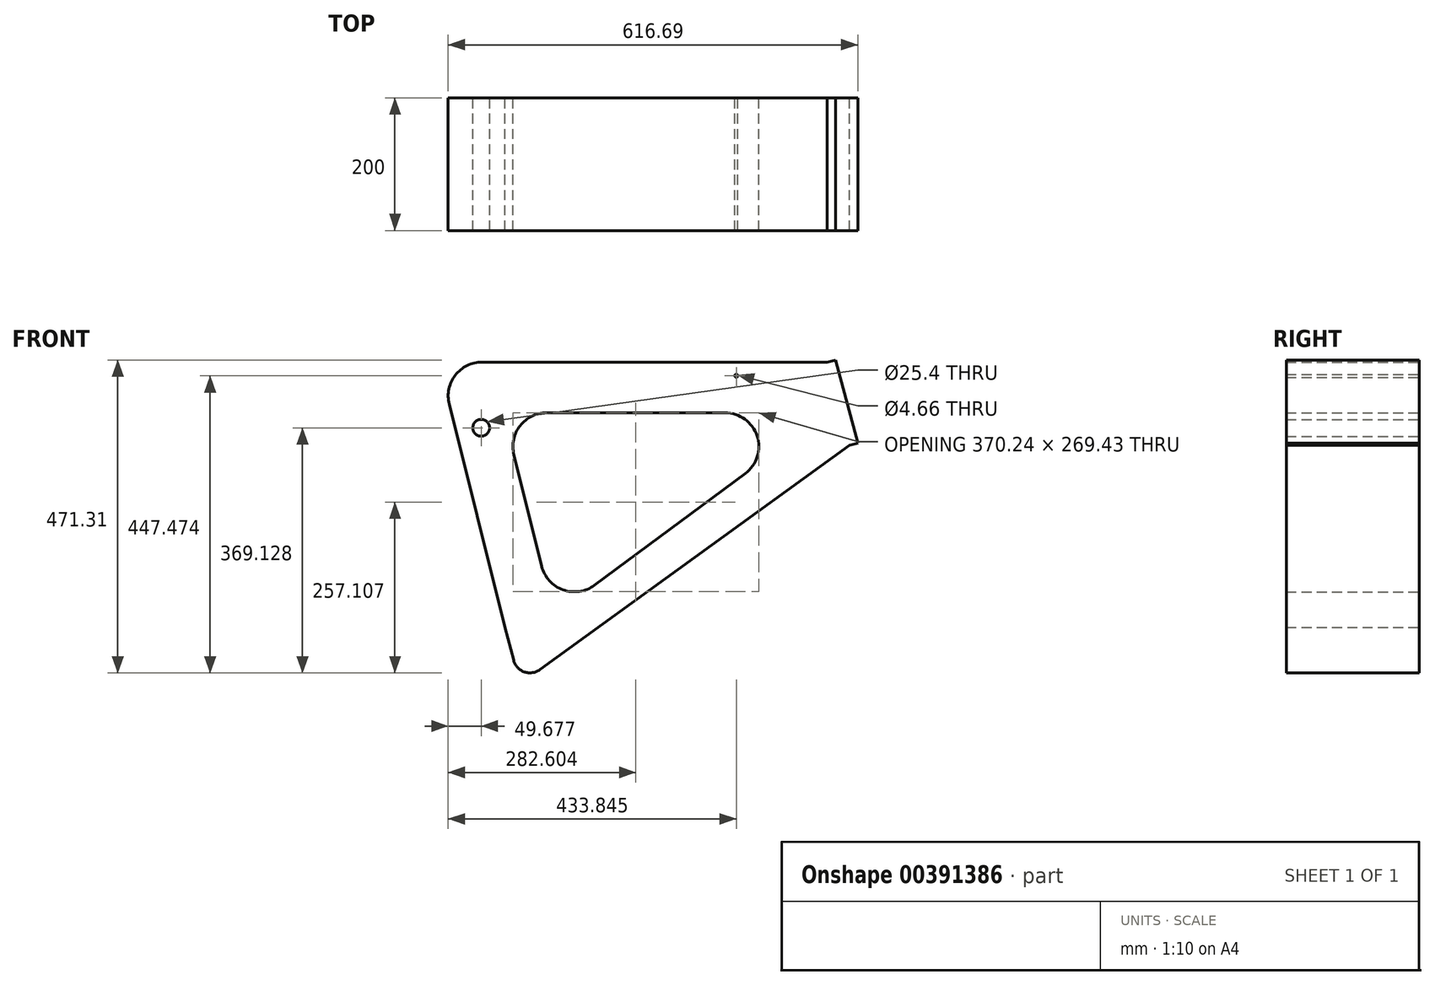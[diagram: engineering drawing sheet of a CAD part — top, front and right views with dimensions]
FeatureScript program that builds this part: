
annotation { "Feature Type Name" : "Feature", "Feature Type Description" : "" }
export const myFeature = defineFeature(function(context is Context, id is Id, definition is map)
    precondition{}
    {
        {
            var Q0;
            Q0=qCreatedBy(makeId("Front.planeOp"),FACE);
            var sketch = newSketch(context, id + "F0", { "sketchPlane" : qUnion([Q0])});
            skLineSegment(sketch, "E0", {"start": v(-464.4, 28.31) * mm, "end": v(55.62, 28.31) * mm});
            skLineSegment(sketch, "E1", {"start": v(89.22, -97.1) * mm, "end": v(-377.27, -434.88) * mm});
            skLineSegment(sketch, "E2", {"start": v(-416.7, -420.88) * mm, "end": v(-429.99, -371.3) * mm});
            skLineSegment(sketch, "E3", {"start": v(55.62, 28.31) * mm, "end": v(55.62, -121.44) * mm, "construction": true});
            skLineSegment(sketch, "E4", {"start": v(-513.7, -34.75) * mm, "end": v(-429.99, -371.3) * mm});
            skCircle(sketch, "E5", {"center": v(-81.35, 7.76) * mm, "radius": 2.33 * mm});
            skPoint(sketch, "E6.visualSharp", {"position": v(-407.15, -456.52) * mm});
            skArc(sketch, "E6.filletArc", {"start": v(-416.7, -420.88) * mm, "mid": v(-400.66, -438.25) * mm, "end": v(-377.27, -434.88) * mm});
            skCircle(sketch, "E7", {"center": v(-407.15, -456.52) * mm, "radius": 18 * mm});
            skLineSegment(sketch, "E8", {"start": v(55.62, 28.31) * mm, "end": v(89.22, -97.1) * mm});
            skLineSegment(sketch, "E9.0", {"start": v(67.89, 31.6) * mm, "end": v(101.5, -93.82) * mm});
            skLineSegment(sketch, "E10", {"start": v(55.62, 28.31) * mm, "end": v(67.89, 31.6) * mm});
            skLineSegment(sketch, "E11", {"start": v(89.22, -97.1) * mm, "end": v(101.5, -93.82) * mm});
            skLineSegment(sketch, "E12", {"start": v(67.89, 31.6) * mm, "end": v(66.57, 36.5) * mm});
            skLineSegment(sketch, "E13", {"start": v(66.57, 36.5) * mm, "end": v(96.01, 44.4) * mm});
            skLineSegment(sketch, "E14", {"start": v(96.01, 44.4) * mm, "end": v(132.25, -90.84) * mm});
            skLineSegment(sketch, "E15", {"start": v(132.25, -90.84) * mm, "end": v(102.8, -98.73) * mm});
            skLineSegment(sketch, "E16", {"start": v(102.8, -98.73) * mm, "end": v(101.5, -93.82) * mm});
            skLineSegment(sketch, "E17", {"start": v(81.3, 40.45) * mm, "end": v(117.53, -94.78) * mm, "construction": true});
            skLineSegment(sketch, "E18.0", {"start": v(-366.92, -47.89) * mm, "end": v(-98.27, -47.89) * mm});
            skLineSegment(sketch, "E18.1", {"start": v(-416.22, -110.95) * mm, "end": v(-374.42, -279.03) * mm});
            skLineSegment(sketch, "E19", {"start": v(-294.88, -307.58) * mm, "end": v(-68.03, -139.5) * mm});
            skCircle(sketch, "E20", {"center": v(-407.15, -456.52) * mm, "radius": 63.5 * mm, "construction": true});
            skArc(sketch, "E21.0", {"start": v(-335.15, -404.38) * mm, "mid": v(-377.4, -372.74) * mm, "end": v(-430.15, -370.65) * mm, "construction": true});
            skCircle(sketch, "E22", {"center": v(-407.15, -456.52) * mm, "radius": 44.8 * mm, "construction": true});
            skPoint(sketch, "E23.visualSharp", {"position": v(-431.9, -47.89) * mm});
            skArc(sketch, "E23.filletArc", {"start": v(-366.92, -47.89) * mm, "mid": v(-406.95, -67.4) * mm, "end": v(-416.22, -110.95) * mm});
            skPoint(sketch, "E24.visualSharp", {"position": v(-356.04, -352.9) * mm});
            skArc(sketch, "E24.filletArc", {"start": v(-374.42, -279.03) * mm, "mid": v(-342.28, -314.58) * mm, "end": v(-294.88, -307.58) * mm});
            skPoint(sketch, "E25.visualSharp", {"position": v(55.62, -47.89) * mm});
            skArc(sketch, "E25.filletArc", {"start": v(-68.03, -139.5) * mm, "mid": v(-50.04, -82.77) * mm, "end": v(-98.27, -47.89) * mm});
            skPoint(sketch, "E26.visualSharp", {"position": v(-529.38, 28.31) * mm});
            skArc(sketch, "E26.filletArc", {"start": v(-464.4, 28.31) * mm, "mid": v(-504.42, 8.8) * mm, "end": v(-513.7, -34.75) * mm});
            skLineSegment(sketch, "E27", {"start": v(-471.84, -203.02) * mm, "end": v(-397.9, -184.63) * mm, "construction": true});
            skLineSegment(sketch, "E28", {"start": v(-434.87, -193.83) * mm, "end": v(-465.52, -70.58) * mm, "construction": true});
            skCircle(sketch, "E29", {"center": v(-465.52, -70.58) * mm, "radius": 12.7 * mm});
            skSolve(sketch);
        }
        {
            var Q0;
            Q0=makeQuery(id+"F0.imprint","IMPRINT",FACE,{"disambiguationData":[TD([[makeQuery(id+"F0.imprint","IMPRINT",EDGE,{"derivedFrom":sQuery(id+"F0.wireOp",EDGE,"E0")}),-1.0]])]});
            extrude(context, id + "F1", {"entities" : qUnion([Q0]), "depth" : 100 * mm, "offsetDistance" : 25.4 * mm, "hasSecondDirection" : true, "secondDirectionOppositeDirection" : true, "secondDirectionDepth" : 100 * mm});
        }
        {
            var Q0;
            Q0=makeQuery(id+"F0.imprint","IMPRINT",FACE,{"disambiguationData":[TD([[makeQuery(id+"F0.imprint","IMPRINT",EDGE,{"derivedFrom":sQuery(id+"F0.wireOp",EDGE,"E8")}),1.0]])]});
            extrude(context, id + "F2", {"entities" : qUnion([Q0]), "operationType" : NewBodyOperationType.ADD, "depth" : 100 * mm, "offsetDistance" : 25.4 * mm, "hasSecondDirection" : true, "secondDirectionOppositeDirection" : true, "secondDirectionDepth" : 100 * mm});
        }
    });
